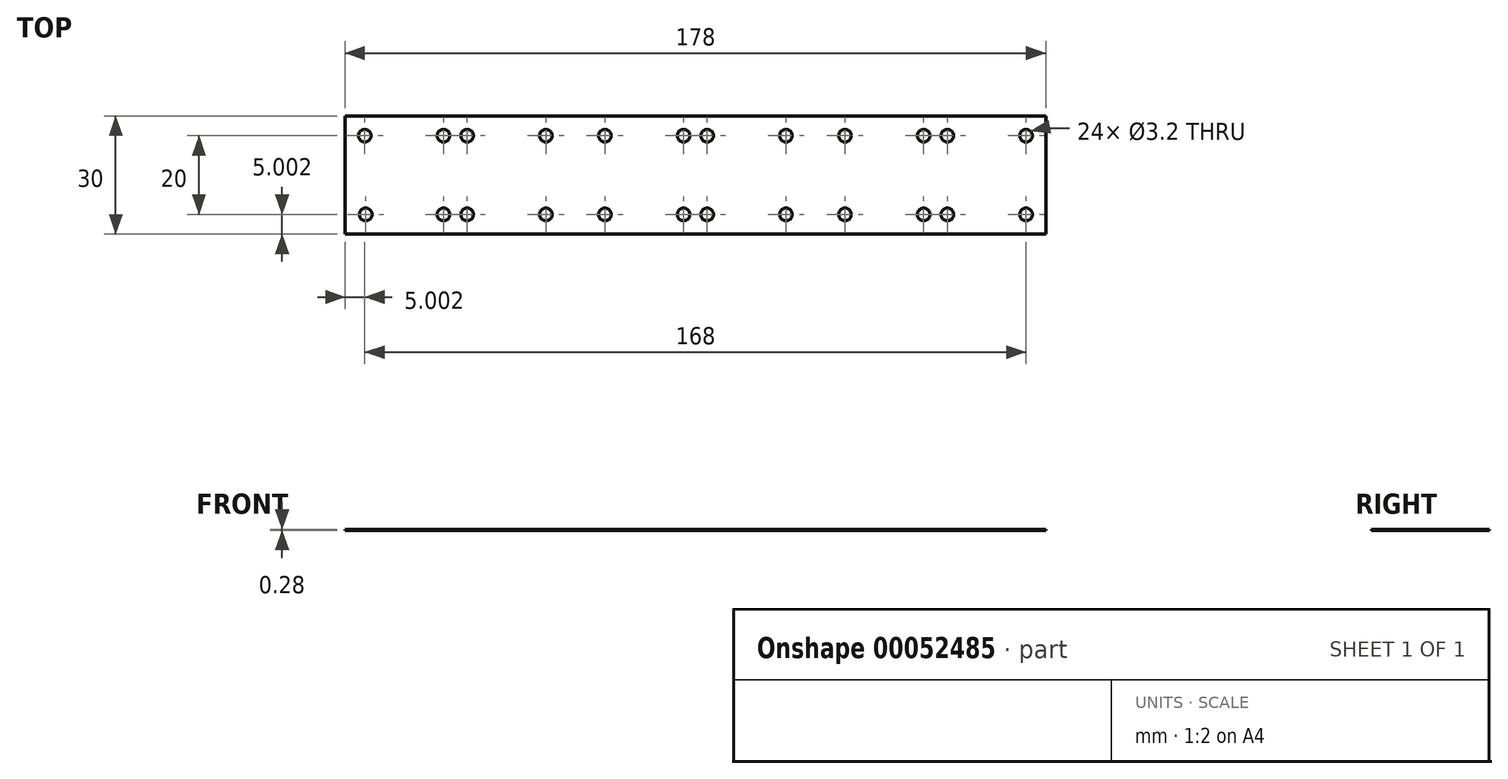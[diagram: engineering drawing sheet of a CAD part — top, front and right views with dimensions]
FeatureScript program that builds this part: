
annotation { "Feature Type Name" : "Feature", "Feature Type Description" : "" }
export const myFeature = defineFeature(function(context is Context, id is Id, definition is map)
    precondition{}
    {
        {
            var Q0;
            Q0=qCreatedBy(makeId("Top.planeOp"),FACE);
            var sketch = newSketch(context, id + "F0", { "sketchPlane" : qUnion([Q0])});
            skCircle(sketch, "E0", {"center": v(-123.59, 17.2) * mm, "radius": 1.6 * mm});
            skCircle(sketch, "E1", {"center": v(-123.36, -2.8) * mm, "radius": 1.6 * mm});
            skCircle(sketch, "E2", {"center": v(-103.59, -2.8) * mm, "radius": 1.6 * mm});
            skCircle(sketch, "E3", {"center": v(-103.59, 17.2) * mm, "radius": 1.6 * mm});
            skCircle(sketch, "E4", {"center": v(-77.59, 17.2) * mm, "radius": 1.6 * mm});
            skCircle(sketch, "E5", {"center": v(-97.59, 17.2) * mm, "radius": 1.6 * mm});
            skCircle(sketch, "E6", {"center": v(-97.59, -2.8) * mm, "radius": 1.6 * mm});
            skCircle(sketch, "E7", {"center": v(-77.59, -2.8) * mm, "radius": 1.6 * mm});
            skCircle(sketch, "E8", {"center": v(-62.59, -2.8) * mm, "radius": 1.6 * mm});
            skCircle(sketch, "E9", {"center": v(-62.59, 17.2) * mm, "radius": 1.6 * mm});
            skCircle(sketch, "E10", {"center": v(-36.59, 17.2) * mm, "radius": 1.6 * mm});
            skCircle(sketch, "E11", {"center": v(-16.59, 17.2) * mm, "radius": 1.6 * mm});
            skCircle(sketch, "E12", {"center": v(-42.59, -2.8) * mm, "radius": 1.6 * mm});
            skCircle(sketch, "E13", {"center": v(-16.59, -2.8) * mm, "radius": 1.6 * mm});
            skCircle(sketch, "E14", {"center": v(-42.59, 17.2) * mm, "radius": 1.6 * mm});
            skCircle(sketch, "E15", {"center": v(-36.59, -2.8) * mm, "radius": 1.6 * mm});
            skCircle(sketch, "E16", {"center": v(-1.59, -2.8) * mm, "radius": 1.6 * mm});
            skCircle(sketch, "E17", {"center": v(24.41, 17.2) * mm, "radius": 1.6 * mm});
            skCircle(sketch, "E18", {"center": v(24.41, -2.8) * mm, "radius": 1.6 * mm});
            skCircle(sketch, "E19", {"center": v(44.41, -2.8) * mm, "radius": 1.6 * mm});
            skCircle(sketch, "E20", {"center": v(18.41, 17.2) * mm, "radius": 1.6 * mm});
            skCircle(sketch, "E21", {"center": v(18.41, -2.8) * mm, "radius": 1.6 * mm});
            skCircle(sketch, "E22", {"center": v(-1.59, 17.2) * mm, "radius": 1.6 * mm});
            skCircle(sketch, "E23", {"center": v(44.41, 17.2) * mm, "radius": 1.6 * mm});
            skLineSegment(sketch, "E24.bottom", {"start": v(-128.59, 22.2) * mm, "end": v(49.41, 22.2) * mm});
            skLineSegment(sketch, "E24.top", {"start": v(-128.59, -7.8) * mm, "end": v(49.41, -7.8) * mm});
            skLineSegment(sketch, "E24.left", {"start": v(-128.59, 22.2) * mm, "end": v(-128.59, -7.8) * mm});
            skLineSegment(sketch, "E24.right", {"start": v(49.41, 22.2) * mm, "end": v(49.41, -7.8) * mm});
            skSolve(sketch);
        }
        {
            var Q0;
            Q0 = qSketchRegion(id + "F0", true);
            extrude(context, id + "F1", {"entities" : qUnion([Q0]), "depth" : .282222 * mm});
        }
    });
